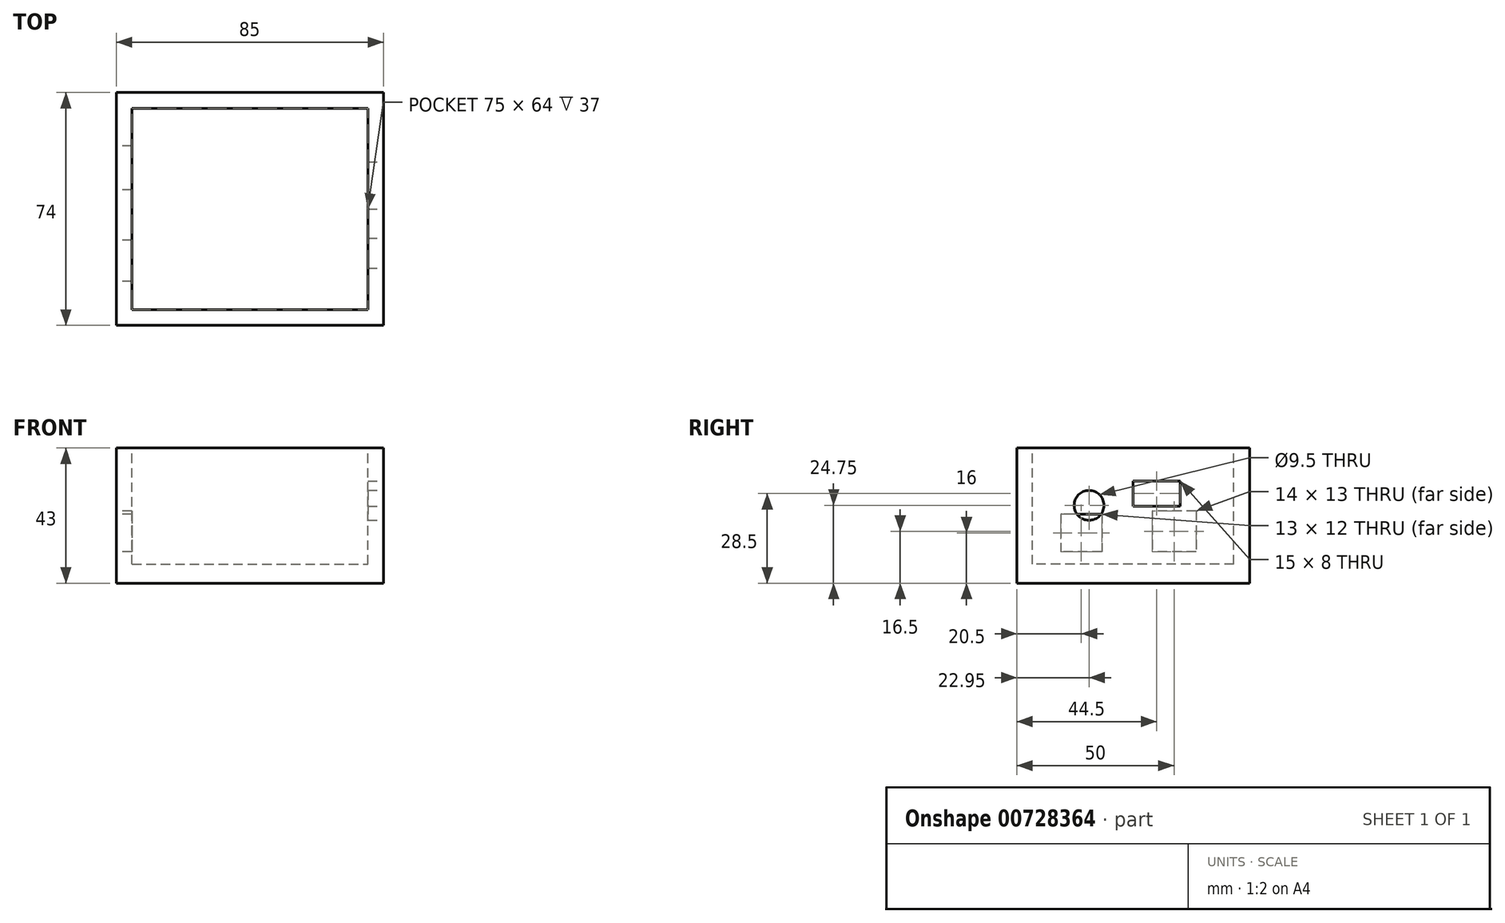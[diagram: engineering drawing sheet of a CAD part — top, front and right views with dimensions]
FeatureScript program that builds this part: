
annotation { "Feature Type Name" : "Feature", "Feature Type Description" : "" }
export const myFeature = defineFeature(function(context is Context, id is Id, definition is map)
    precondition{}
    {
        {
            var Q0;
            Q0=qCreatedBy(makeId("Top.planeOp"),FACE);
            var sketch = newSketch(context, id + "F0", { "sketchPlane" : qUnion([Q0])});
            skLineSegment(sketch, "E0.bottom", {"start": v(-42.5, 37) * mm, "end": v(42.5, 37) * mm});
            skLineSegment(sketch, "E0.top", {"start": v(-42.5, -37) * mm, "end": v(42.5, -37) * mm});
            skLineSegment(sketch, "E0.left", {"start": v(-42.5, 37) * mm, "end": v(-42.5, -37) * mm});
            skLineSegment(sketch, "E0.right", {"start": v(42.5, 37) * mm, "end": v(42.5, -37) * mm});
            skPoint(sketch, "E0.middle", {"position": v(0, 0) * mm});
            skSolve(sketch);
        }
        {
            var Q0;
            Q0=makeQuery(id+"F0.imprint","IMPRINT",FACE,{"disambiguationData":[TD([[makeQuery(id+"F0.imprint","IMPRINT",EDGE,{"derivedFrom":sQuery(id+"F0.wireOp",EDGE,"E0.bottom")}),-1.0]])]});
            extrude(context, id + "F1", {"entities" : qUnion([Q0]), "depth" : 43 * mm, "offsetDistance" : 25.4 * mm});
        }
        {
            var Q0;
            Q0=makeQuery(id+"F1.opExtrude","CAP_FACE",FACE,{"disambiguationData":[OSD([sQuery(id+"F0.wireOp",EDGE,"E0.bottom"),sQuery(id+"F0.wireOp",EDGE,"E0.top"),sQuery(id+"F0.wireOp",EDGE,"E0.left"),sQuery(id+"F0.wireOp",EDGE,"E0.right")])],"isStart":false});
            var sketch = newSketch(context, id + "F2", { "sketchPlane" : qUnion([Q0])});
            skLineSegment(sketch, "E1.bottom", {"start": v(-37.5, 32) * mm, "end": v(37.5, 32) * mm});
            skLineSegment(sketch, "E1.top", {"start": v(-37.5, -32) * mm, "end": v(37.5, -32) * mm});
            skLineSegment(sketch, "E1.left", {"start": v(-37.5, 32) * mm, "end": v(-37.5, -32) * mm});
            skLineSegment(sketch, "E1.right", {"start": v(37.5, 32) * mm, "end": v(37.5, -32) * mm});
            skPoint(sketch, "E1.middle", {"position": v(0, 0) * mm});
            skSolve(sketch);
        }
        {
            var Q0;
            Q0=makeQuery(id+"F2.imprint","IMPRINT",FACE,{"disambiguationData":[TD([[makeQuery(id+"F2.imprint","IMPRINT",EDGE,{"derivedFrom":sQuery(id+"F2.wireOp",EDGE,"E1.bottom")}),-1.0]])]});
            extrude(context, id + "F3", {"entities" : qUnion([Q0]), "operationType" : NewBodyOperationType.REMOVE, "oppositeDirection" : true, "depth" : 37 * mm, "offsetDistance" : 25.4 * mm});
        }
        {
            var Q0;
            Q0=makeQuery(id+"F1.opExtrude","SWEPT_FACE",FACE,{"disambiguationData":[OSD([sQuery(id+"F0.wireOp",EDGE,"E0.right")])]});
            var sketch = newSketch(context, id + "F4", { "sketchPlane" : qUnion([Q0])});
            skLineSegment(sketch, "E2.bottom", {"start": v(0, 32.5) * mm, "end": v(15, 32.5) * mm});
            skLineSegment(sketch, "E2.top", {"start": v(0, 24.5) * mm, "end": v(15, 24.5) * mm});
            skLineSegment(sketch, "E2.left", {"start": v(0, 32.5) * mm, "end": v(0, 24.5) * mm});
            skLineSegment(sketch, "E2.right", {"start": v(15, 32.5) * mm, "end": v(15, 24.5) * mm});
            skSolve(sketch);
        }
        {
            var Q0;
            Q0=makeQuery(id+"F4.imprint","IMPRINT",FACE,{"disambiguationData":[TD([[makeQuery(id+"F4.imprint","IMPRINT",EDGE,{"derivedFrom":sQuery(id+"F4.wireOp",EDGE,"E2.bottom")}),-1.0]])]});
            extrude(context, id + "F5", {"entities" : qUnion([Q0]), "operationType" : NewBodyOperationType.REMOVE, "oppositeDirection" : true, "depth" : 6 * mm, "offsetDistance" : 25.4 * mm});
        }
        {
            var Q0;
            Q0=makeQuery(id+"F1.opExtrude","SWEPT_FACE",FACE,{"disambiguationData":[OSD([sQuery(id+"F0.wireOp",EDGE,"E0.right")])]});
            var sketch = newSketch(context, id + "F6", { "sketchPlane" : qUnion([Q0])});
            skCircle(sketch, "E3", {"center": v(-14.05, 24.75) * mm, "radius": 4.75 * mm});
            skSolve(sketch);
        }
        {
            var Q0;
            Q0=makeQuery(id+"F6.imprint","IMPRINT",FACE,{"disambiguationData":[TD([[makeQuery(id+"F6.imprint","IMPRINT",EDGE,{"derivedFrom":sQuery(id+"F6.wireOp",EDGE,"E3")}),1.0]])]});
            extrude(context, id + "F7", {"entities" : qUnion([Q0]), "operationType" : NewBodyOperationType.REMOVE, "oppositeDirection" : true, "depth" : 6 * mm, "offsetDistance" : 25.4 * mm});
        }
        {
            var Q0;
            Q0=makeQuery(id+"F1.opExtrude","SWEPT_FACE",FACE,{"disambiguationData":[OSD([sQuery(id+"F0.wireOp",EDGE,"E0.left")])]});
            var sketch = newSketch(context, id + "F8", { "sketchPlane" : qUnion([Q0])});
            skLineSegment(sketch, "E4.bottom", {"start": v(-20, 23) * mm, "end": v(-6, 23) * mm});
            skLineSegment(sketch, "E4.top", {"start": v(-20, 10) * mm, "end": v(-6, 10) * mm});
            skLineSegment(sketch, "E4.left", {"start": v(-20, 23) * mm, "end": v(-20, 10) * mm});
            skLineSegment(sketch, "E4.right", {"start": v(-6, 23) * mm, "end": v(-6, 10) * mm});
            skSolve(sketch);
        }
        {
            var Q0;
            Q0=makeQuery(id+"F8.imprint","IMPRINT",FACE,{"disambiguationData":[TD([[makeQuery(id+"F8.imprint","IMPRINT",EDGE,{"derivedFrom":sQuery(id+"F8.wireOp",EDGE,"E4.bottom")}),-1.0]])]});
            extrude(context, id + "F9", {"entities" : qUnion([Q0]), "operationType" : NewBodyOperationType.REMOVE, "oppositeDirection" : true, "depth" : 6 * mm, "offsetDistance" : 25.4 * mm});
        }
        {
            var Q0;
            Q0=makeQuery(id+"F1.opExtrude","SWEPT_FACE",FACE,{"disambiguationData":[OSD([sQuery(id+"F0.wireOp",EDGE,"E0.left")])]});
            var sketch = newSketch(context, id + "F10", { "sketchPlane" : qUnion([Q0])});
            skLineSegment(sketch, "E5.bottom", {"start": v(10, 22) * mm, "end": v(23, 22) * mm});
            skLineSegment(sketch, "E5.top", {"start": v(10, 10) * mm, "end": v(23, 10) * mm});
            skLineSegment(sketch, "E5.left", {"start": v(10, 22) * mm, "end": v(10, 10) * mm});
            skLineSegment(sketch, "E5.right", {"start": v(23, 22) * mm, "end": v(23, 10) * mm});
            skSolve(sketch);
        }
        {
            var Q0;
            Q0=makeQuery(id+"F10.imprint","IMPRINT",FACE,{"disambiguationData":[TD([[makeQuery(id+"F10.imprint","IMPRINT",EDGE,{"derivedFrom":sQuery(id+"F10.wireOp",EDGE,"E5.bottom")}),-1.0]])]});
            extrude(context, id + "F11", {"entities" : qUnion([Q0]), "operationType" : NewBodyOperationType.REMOVE, "oppositeDirection" : true, "depth" : 6 * mm, "offsetDistance" : 25.4 * mm});
        }
    });
